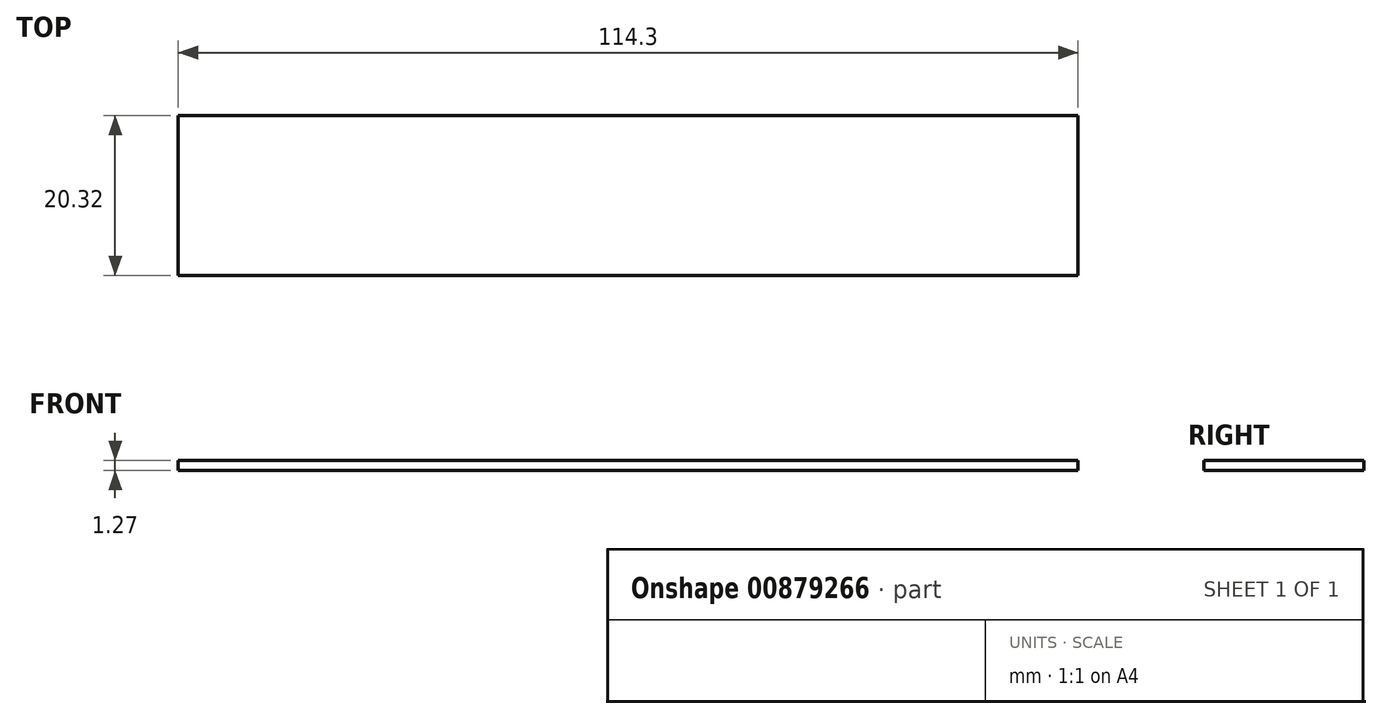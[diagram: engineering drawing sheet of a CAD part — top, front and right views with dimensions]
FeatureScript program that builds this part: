
annotation { "Feature Type Name" : "Feature", "Feature Type Description" : "" }
export const myFeature = defineFeature(function(context is Context, id is Id, definition is map)
    precondition{}
    {
        {
            var Q0;
            Q0=qCreatedBy(makeId("Top.planeOp"),FACE);
            var sketch = newSketch(context, id + "F0", { "sketchPlane" : qUnion([Q0])});
            skLineSegment(sketch, "E0.bottom", {"start": v(-53.63, -20.32) * mm, "end": v(60.67, -20.32) * mm});
            skLineSegment(sketch, "E0.top", {"start": v(-53.63, 0) * mm, "end": v(60.67, 0) * mm});
            skLineSegment(sketch, "E0.left", {"start": v(-53.63, -20.32) * mm, "end": v(-53.63, 0) * mm});
            skLineSegment(sketch, "E0.right", {"start": v(60.67, -20.32) * mm, "end": v(60.67, 0) * mm});
            skSolve(sketch);
        }
        {
            var Q0;
            Q0=makeQuery(id+"F0.imprint","IMPRINT",FACE,{"disambiguationData":[TD([[makeQuery(id+"F0.imprint","IMPRINT",EDGE,{"derivedFrom":sQuery(id+"F0.wireOp",EDGE,"E0.bottom")}),1.0]])]});
            extrude(context, id + "F1", {"entities" : qUnion([Q0]), "depth" : 1.27 * mm, "offsetDistance" : 25.4 * mm});
        }
    });
